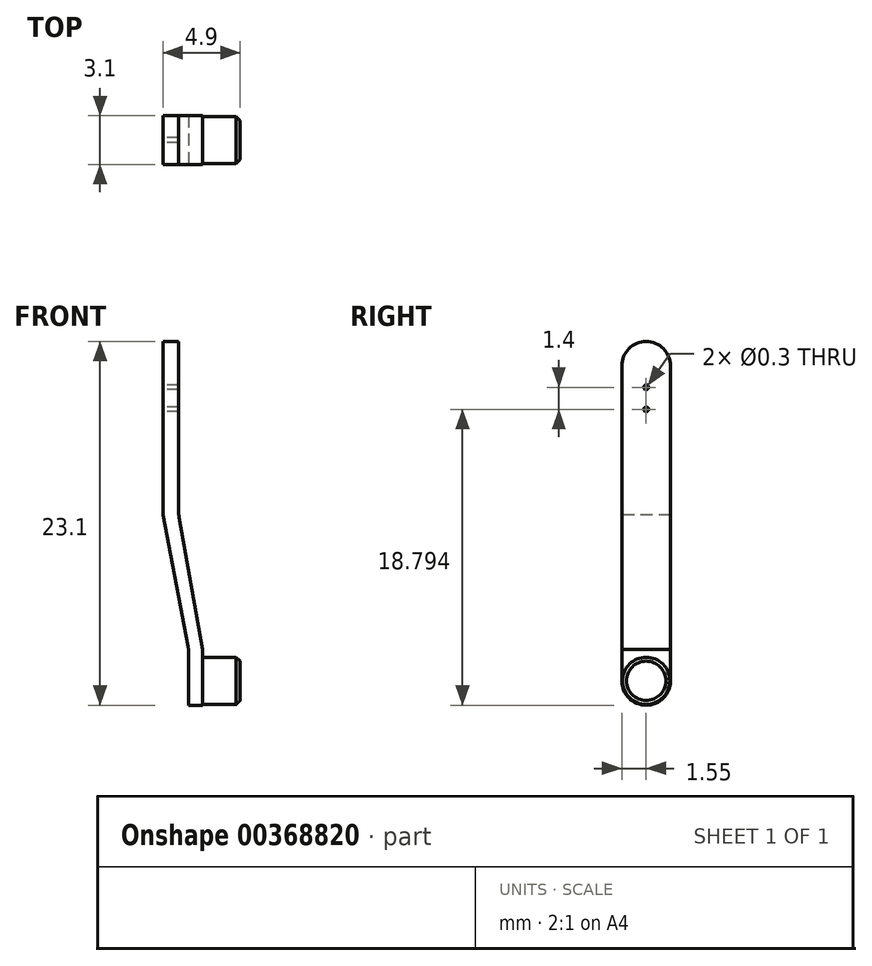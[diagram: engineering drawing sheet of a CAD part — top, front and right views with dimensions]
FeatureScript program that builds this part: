
annotation { "Feature Type Name" : "Feature", "Feature Type Description" : "" }
export const myFeature = defineFeature(function(context is Context, id is Id, definition is map)
    precondition{}
    {
        {
            var Q0;
            Q0=qCreatedBy(makeId("Right.planeOp"),FACE);
            var sketch = newSketch(context, id + "F0", { "sketchPlane" : qUnion([Q0])});
            skLineSegment(sketch, "E0.left", {"start": v(0, 0) * mm, "end": v(0, 20) * mm});
            skLineSegment(sketch, "E0.right", {"start": v(-3.1, 0) * mm, "end": v(-3.1, 20) * mm});
            skArc(sketch, "E1", {"start": v(0, 20) * mm, "mid": v(-1.55, 21.55) * mm, "end": v(-3.1, 20) * mm});
            skArc(sketch, "E2", {"start": v(-3.1, 0) * mm, "mid": v(-1.55, -1.55) * mm, "end": v(0, 0) * mm});
            skCircle(sketch, "E3", {"center": v(-1.55, 18.64) * mm, "radius": 0.15 * mm});
            skCircle(sketch, "E4", {"center": v(-1.55, 17.24) * mm, "radius": 0.15 * mm});
            skSolve(sketch);
        }
        {
            var Q0;
            Q0=makeQuery(id+"F0.imprint","IMPRINT",FACE,{"disambiguationData":[TD([[makeQuery(id+"F0.imprint","IMPRINT",EDGE,{"derivedFrom":sQuery(id+"F0.wireOp",EDGE,"E0.left")}),1.0]])]});
            extrude(context, id + "F1", {"entities" : qUnion([Q0]), "depth" : 2.5 * mm});
        }
        {
            var Q0;
            Q0=makeQuery(id+"F1.opExtrude","CAP_FACE",FACE,{"disambiguationData":[OSD([sQuery(id+"F0.wireOp",EDGE,"E0.left"),sQuery(id+"F0.wireOp",EDGE,"E0.right"),sQuery(id+"F0.wireOp",EDGE,"E1"),sQuery(id+"F0.wireOp",EDGE,"E2"),sQuery(id+"F0.wireOp",EDGE,"E3"),sQuery(id+"F0.wireOp",EDGE,"E4")])],"isStart":false});
            var sketch = newSketch(context, id + "F2", { "sketchPlane" : qUnion([Q0])});
            skCircle(sketch, "E5", {"center": v(-1.55, 0) * mm, "radius": 1.5 * mm});
            skSolve(sketch);
        }
        {
            var Q0;
            Q0=makeQuery(id+"F2.imprint","IMPRINT",FACE,{"disambiguationData":[TD([[makeQuery(id+"F2.imprint","IMPRINT",EDGE,{"derivedFrom":sQuery(id+"F2.wireOp",EDGE,"E5")}),1.0]])]});
            extrude(context, id + "F3", {"entities" : qUnion([Q0]), "operationType" : NewBodyOperationType.ADD, "depth" : 2.4 * mm});
        }
        {
            var Q0;
            Q0=makeQuery(id+"F1.opExtrude","SWEPT_FACE",FACE,{"disambiguationData":[OSD([sQuery(id+"F0.wireOp",EDGE,"E0.right")])]});
            var sketch = newSketch(context, id + "F4", { "sketchPlane" : qUnion([Q0])});
            skLineSegment(sketch, "E6.bottom", {"start": v(2.5, 21.55) * mm, "end": v(1, 21.55) * mm});
            skLineSegment(sketch, "E6.left", {"start": v(2.5, 21.55) * mm, "end": v(2.5, 10.55) * mm});
            skLineSegment(sketch, "E6.right", {"start": v(1, 21.55) * mm, "end": v(1, 10.55) * mm});
            skLineSegment(sketch, "E7", {"start": v(1, 10.55) * mm, "end": v(2.5, 2) * mm});
            skLineSegment(sketch, "E8", {"start": v(2.5, 2) * mm, "end": v(2.5, 10.55) * mm});
            skSolve(sketch);
        }
        {
            var Q0;
            Q0 = qSketchRegion(id + "F4", true);
            extrude(context, id + "F5", {"entities" : qUnion([Q0]), "operationType" : NewBodyOperationType.REMOVE, "oppositeDirection" : true, "depth" : 25 * mm});
        }
        {
            var Q0;
            Q0=makeQuery(id+"F1.opExtrude","SWEPT_FACE",FACE,{"disambiguationData":[OSD([sQuery(id+"F0.wireOp",EDGE,"E0.right")])]});
            var sketch = newSketch(context, id + "F6", { "sketchPlane" : qUnion([Q0])});
            skLineSegment(sketch, "E9", {"start": v(0, 10.55) * mm, "end": v(1.63, 2) * mm});
            skLineSegment(sketch, "E10", {"start": v(1.63, 2) * mm, "end": v(1.63, -2.12) * mm});
            skLineSegment(sketch, "E11", {"start": v(1.63, -2.12) * mm, "end": v(0, -2.12) * mm});
            skLineSegment(sketch, "E12", {"start": v(0, -2.12) * mm, "end": v(0, 10.55) * mm});
            skSolve(sketch);
        }
        {
            var Q0;
            Q0 = qSketchRegion(id + "F6", true);
            extrude(context, id + "F7", {"entities" : qUnion([Q0]), "operationType" : NewBodyOperationType.REMOVE, "oppositeDirection" : true, "depth" : 25 * mm});
        }
        {
            var Q0;
            Q0=makeQuery(id+"F5.boolean.opBoolean","COPY",EDGE,{"derivedFrom":makeQuery(id+"F5.opExtrude","SWEPT_EDGE",EDGE,{"disambiguationData":[OSD([sQuery(id+"F4.wireOp",EDGE,"E6.right"),sQuery(id+"F4.wireOp",EDGE,"E7")])]})});
            var Q1;
            Q1=makeQuery(id+"F5.boolean.opBoolean","COPY",EDGE,{"derivedFrom":makeQuery(id+"F5.opExtrude","SWEPT_EDGE",EDGE,{"disambiguationData":[OSD([sQuery(id+"F0.wireOp",EDGE,"E0.right"),sQuery(id+"F4.wireOp",EDGE,"E7"),sQuery(id+"F4.wireOp",EDGE,"E8")])]})});
            var Q2;
            Q2=makeQuery(id+"F7.boolean.opBoolean","COPY",EDGE,{"derivedFrom":makeQuery(id+"F7.opExtrude","SWEPT_EDGE",EDGE,{"disambiguationData":[OSD([sQuery(id+"F6.wireOp",EDGE,"E9"),sQuery(id+"F6.wireOp",EDGE,"E10")])]})});
            var Q3;
            Q3=makeQuery(id+"F7.boolean.opBoolean","COPY",EDGE,{"derivedFrom":makeQuery(id+"F7.opExtrude","SWEPT_EDGE",EDGE,{"disambiguationData":[OSD([sQuery(id+"F0.wireOp",EDGE,"E0.right"),sQuery(id+"F6.wireOp",EDGE,"E9"),sQuery(id+"F6.wireOp",EDGE,"E12")])]})});
            fillet(context, id + "F8", {"entities" : qUnion([Q0, Q1, Q2, Q3]), "radius" : 2 * mm, "tangentPropagation" : true, "allowEdgeOverflow" : false});
        }
        {
            var Q0;
            Q0=makeQuery(id+"F3.opExtrude","CAP_EDGE",EDGE,{"disambiguationData":[OSD([sQuery(id+"F2.wireOp",EDGE,"E5")])],"isStart":false});
            chamfer(context, id + "F9", {"entities" : qUnion([Q0]), "width" : 0.25 * mm, "tangentPropagation" : true});
        }
    });
